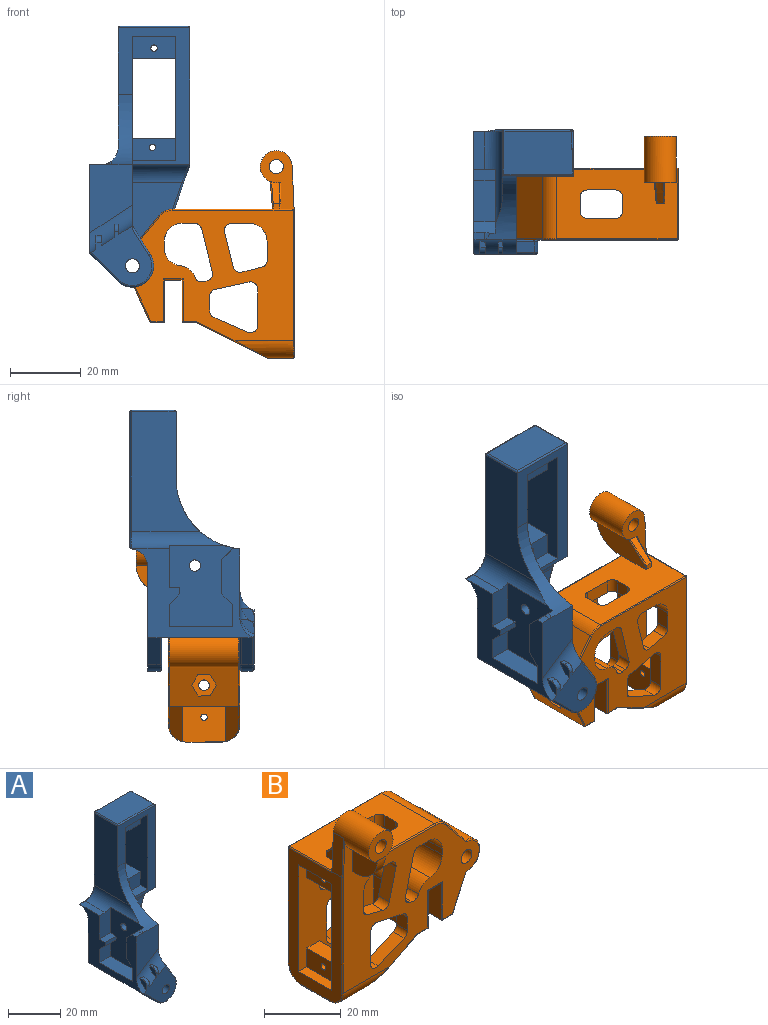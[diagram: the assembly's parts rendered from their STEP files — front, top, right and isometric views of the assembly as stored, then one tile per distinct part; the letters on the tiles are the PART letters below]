
ASSEMBLY  parts=2 mates=1
PART A: 94 faces, bbox 31.5x35.5x74.7 mm
  f0: cylinder r=5mm len=25.96mm, axis (0,1,0), area 138.7mm2, adj f4,f16,f24,f37,f64,f82
  f1: plane 3x2.1mm, normal (0,0,1), area 6.3mm2, adj f3,f12,f15,f67
  f2: plane 29.49x26.47mm, normal (0,1,0), area 568.4mm2, adj f12,f34,f35,f36,f43,f68
  f3: plane 19.15x12mm, normal (0,-1,0), area 182.8mm2, adj f1,f10,f12,f64,f65
  f4: plane 10.6x3mm, normal (0,0,1), area 31.8mm2, adj f0,f12,f16,f83
  f5: plane 29.09x25.27mm, normal (0,-1,0), area 313.8mm2, adj f10,f13,f32,f43,f66,f76,f77,f78
  f6: plane 12.2x6.25mm, normal (0,-1,0), area 73.7mm2, adj f39,f40,f42,f47,f51
  f7: plane 12.2x6.25mm, normal (0,-1,0), area 73.7mm2, adj f38,f39,f42,f48,f50
  f8: plane 22.5x0.08mm, normal (0,1,0), area 1.9mm2, adj f38,f40,f42,f44
  f9: plane 38.94x0.08mm, normal (0,1,0), area 3.2mm2, adj f33,f34,f45,f86
  f10: plane 42.72x26.34mm, normal (1,0,0), area 549.7mm2, adj f3,f5,f26,f27,f28,f29,f30,f31
  f11: cylinder r=1.6mm len=3.2mm, axis (-1,0,0), area 32.2mm2, adj f24,f25
  f12: plane 34.36x25.03mm, normal (-1,0,0), area 317.3mm2, adj f1,f2,f3,f4,f13,f14,f15,f16
  f13: plane 23.21x7.33mm, normal (0,0,-1), area 156.8mm2, adj f5,f12,f32,f63,f74,f78
  f14: plane 9.7x6mm, normal (0,1,0), area 58.2mm2, adj f12,f15,f23,f24
  f15: plane 6.13x3.4mm, normal (0,0.71,0.71), area 26.2mm2, adj f1,f12,f14,f24,f64,f67
  f16: plane 12x6mm, normal (0,-1,0), area 67mm2, adj f0,f4,f12,f17,f24
  f17: plane 6x3mm, normal (0,0,1), area 18mm2, adj f12,f16,f18,f24
  f18: plane 6x1.7mm, normal (0,-1,0), area 10.2mm2, adj f12,f17,f19,f24
  f19: plane 6x3mm, normal (0,-0.71,-0.71), area 25.5mm2, adj f12,f18,f20,f24
  f20: plane 6.3x6mm, normal (0,-1,0), area 37.8mm2, adj f12,f19,f21,f24
  f21: plane 17.8x6mm, normal (0,0,1), area 106.8mm2, adj f12,f20,f22,f24
  f22: plane 6.3x6mm, normal (0,1,0), area 37.8mm2, adj f12,f21,f23,f24
  f23: plane 6x3mm, normal (0,0.71,-0.71), area 25.5mm2, adj f12,f14,f22,f24
  f24: plane 23x18.07mm, normal (-1,0,0), area 352.8mm2, adj f0,f11,f14,f15,f16,f17,f18,f19
  f25: plane 6.81x5.9mm, normal (1,0,0), area 22.1mm2, adj f11,f26,f27,f28,f29,f30,f31
  f26: plane 2.95x2.8mm, normal (0,-0.5,-0.87), area 9.5mm2, adj f10,f25,f27,f31
  f27: plane 2.95x2.8mm, normal (0,0.5,-0.87), area 9.5mm2, adj f10,f25,f26,f28
  f28: plane 3.41x2.8mm, normal (0,1,0), area 9.5mm2, adj f10,f25,f27,f29
  f29: plane 2.95x2.8mm, normal (0,0.5,0.87), area 9.5mm2, adj f10,f25,f28,f30
  f30: plane 2.95x2.8mm, normal (0,-0.5,0.87), area 9.5mm2, adj f10,f25,f29,f31
  f31: plane 3.41x2.8mm, normal (0,-1,0), area 9.5mm2, adj f10,f25,f26,f30
  f32: cylinder r=6mm len=22mm, axis (0,1,0), area 125.4mm2, adj f5,f10,f13,f63
  f33: plane 38.79x8.09mm, normal (1,0,0), area 309.5mm2, adj f9,f34,f49,f75,f88
  f34: plane 30.45x10.53mm, normal (0.95,0,-0.33), area 122.4mm2, adj f2,f9,f33,f35,f45,f68,f75,f76
  f35: cylinder r=6mm len=9.91mm, axis (0,-1,0), area 42.5mm2, adj f2,f34,f36,f77
  f36: plane 7.76x7.74mm, normal (-0.71,0,-0.71), area 38.4mm2, adj f2,f12,f35,f78
  f37: plane 33.7x19.16mm, normal (-1,0,0), area 451.7mm2, adj f0,f49,f64,f80,f92
  f38: plane 12.28x9mm, normal (0,0,1), area 110.2mm2, adj f7,f8,f39,f42,f44,f46
  f39: plane 35x13mm, normal (-1,0,0), area 342.5mm2, adj f6,f7,f38,f40,f46,f47,f48,f49
  f40: plane 12.28x9mm, normal (0,0,-1), area 110.2mm2, adj f6,f8,f39,f42,f44,f46
  f41: plane 19.2x12mm, normal (0,0,1), area 230mm2, adj f86,f87,f88,f90,f91,f92
  f42: plane 35x8mm, normal (1,0,0), area 230mm2, adj f6,f7,f8,f10,f38,f40,f47,f48
  f43: cylinder r=2mm len=4mm, axis (0,-1,0), area 50.3mm2, adj f2,f5
  f44: plane 22.5x5mm, normal (1,0,0), area 112.5mm2, adj f8,f38,f40,f46
  f45: plane 38.94x4.5mm, normal (1,0,0), area 175.1mm2, adj f9,f34,f68,f79,f87
  f46: plane 38.22x21.49mm, normal (0,1,0), area 452.4mm2, adj f38,f39,f40,f44,f50,f51,f79,f80
  f47: plane 12.2x4mm, normal (0,0,-1), area 48.8mm2, adj f6,f39,f42,f49
  f48: plane 12.2x4mm, normal (0,0,1), area 48.8mm2, adj f7,f39,f42,f49
  f49: plane 38.71x20.22mm, normal (0,-1,0), area 275.1mm2, adj f10,f33,f37,f39,f42,f47,f48,f64
  f50: cylinder r=0.9mm len=9mm, axis (0,-1,0), area 50.9mm2, adj f7,f46
  f51: cylinder r=0.9mm len=9mm, axis (0,-1,0), area 50.9mm2, adj f6,f46
  f52: plane 8.14x5.09mm, normal (0.85,0,0.53), area 28.8mm2, adj f10,f60,f69,f72
  f53: plane 3.89x3.5mm, normal (1,0,0), area 5.8mm2, adj f54,f62,f65,f85
  f54: plane 1.74x1.34mm, normal (0,0,1), area 2.1mm2, adj f53,f55,f65,f85
  f55: plane 3.87x3.72mm, normal (-1,0,0), area 8.9mm2, adj f54,f62,f65,f85
  f56: plane 3.76x3.27mm, normal (1,0,0), area 5.2mm2, adj f57,f62,f65,f84
  f57: plane 1.74x1.62mm, normal (0,0,1), area 2.4mm2, adj f56,f58,f65,f84
  f58: plane 3.85x3.71mm, normal (-1,0,0), area 8.9mm2, adj f57,f62,f65,f84
  f59: plane 7.76x7.73mm, normal (-0.71,0,-0.71), area 32.9mm2, adj f12,f60,f71,f74
  f60: cylinder r=6mm len=10.24mm, axis (0,1,0), area 52.5mm2, adj f52,f59,f70,f73
  f61: cylinder r=1.98mm len=4mm, axis (0,1,0), area 49.8mm2, adj f62,f63
  f62: plane 17.07x16.82mm, normal (0,-1,0), area 155.3mm2, adj f10,f53,f55,f56,f58,f61,f65,f69
  f63: plane 16.79x15.88mm, normal (0,1,0), area 113mm2, adj f10,f13,f32,f61,f72,f73,f74
  f64: cylinder r=20mm len=19.9mm, axis (-1,0,0), area 139mm2, adj f0,f3,f10,f15,f24,f37,f49,f67
  f65: cylinder r=5mm len=17.32mm, axis (0.84,0,0.55), area 80.4mm2, adj f3,f10,f12,f53,f54,f55,f56,f57
  f66: cylinder r=5mm len=15.84mm, axis (-1,0,0), area 102.1mm2, adj f5,f10,f49,f75
  f67: cylinder r=5mm len=2.1mm, axis (0,1,0), area 1.7mm2, adj f1,f15,f64
  f68: cylinder r=5mm len=28.12mm, axis (-1,0,0), area 203.7mm2, adj f2,f12,f34,f45,f79,f81
  f69: cylinder r=0.5mm len=8.41mm, axis (0.53,0,-0.85), area 7.2mm2, adj f10,f52,f62,f70
  f70: torus R=5.5mm, axis (0,-1,0), area 13.3mm2, adj f60,f62,f69,f71
  f71: cylinder r=0.5mm len=8.15mm, axis (-0.71,0,0.71), area 8.6mm2, adj f12,f59,f62,f65,f70
  f72: cylinder r=0.5mm len=8.41mm, axis (-0.53,0,0.85), area 7.2mm2, adj f10,f52,f63,f73
  f73: torus R=5.5mm, axis (0,-1,0), area 13.3mm2, adj f60,f63,f72,f74
  f74: cylinder r=0.5mm len=8.11mm, axis (0.71,0,-0.71), area 8.4mm2, adj f13,f59,f63,f73
  f75: bspline ~6.44x5.06mm, area 5mm2, adj f33,f34,f49,f66,f76
  f76: cylinder r=0.5mm len=25.55mm, axis (-0.33,0,-0.95), area 21.1mm2, adj f5,f34,f75,f77
  f77: torus R=5.5mm, axis (0,1,0), area 9.2mm2, adj f5,f35,f76,f78
  f78: cylinder r=0.5mm len=8.12mm, axis (-0.71,0,0.71), area 8.4mm2, adj f5,f13,f36,f77
  f79: cylinder r=0.5mm len=38.73mm, axis (0,0,1), area 30.3mm2, adj f45,f46,f68,f81,f89
  f80: cylinder r=0.5mm len=33.7mm, axis (0,0,-1), area 26.5mm2, adj f37,f46,f82,f93
  f81: cylinder r=0.5mm len=28.11mm, axis (-1,0,0), area 17.4mm2, adj f12,f46,f68,f79,f82,f83
  f82: torus R=5.5mm, axis (0,1,0), area 5.1mm2, adj f0,f46,f80,f81,f83
  f83: cylinder r=0.5mm len=3mm, axis (-1,0,0), area 0.3mm2, adj f4,f12,f81,f82
  f84: cylinder r=2mm len=2mm, axis (1,0,0), area 5mm2, adj f56,f57,f58,f62
  f85: cylinder r=2mm len=2mm, axis (1,0,0), area 4.1mm2, adj f53,f54,f55,f62
  f86: cylinder r=0.5mm len=0.58mm, axis (-1,0,0), area 0.1mm2, adj f9,f41,f87,f88
  f87: cylinder r=0.5mm len=5mm, axis (0,1,0), area 3.7mm2, adj f41,f45,f86,f89
  f88: cylinder r=0.5mm len=8mm, axis (0,1,0), area 5.9mm2, adj f33,f41,f86,f90
  f89: sphere r=0.5mm, area 0.5mm2, adj f79,f87,f91
  f90: cylinder r=0.5mm len=20.2mm, axis (1,0,0), area 15.5mm2, adj f41,f49,f88,f92
  f91: cylinder r=0.5mm len=19.12mm, axis (-1,0,0), area 15mm2, adj f41,f46,f89,f93
  f92: cylinder r=0.5mm len=12.5mm, axis (0,-1,0), area 9.6mm2, adj f37,f41,f90,f93
  f93: sphere r=0.5mm, area 0.2mm2, adj f80,f91,f92
PART B: 139 faces, bbox 51.1x29.6x58.9 mm
  f0: plane 33.98x19.61mm, normal (0,0,1), area 537.5mm2, adj f8,f32,f50,f52,f53,f90,f91,f102
  f1: plane 20.2x19mm, normal (0,0,-1), area 208.1mm2, adj f2,f3,f4,f5,f28,f29,f111,f112
  f2: plane 37.9x28.06mm, normal (0,1,0), area 524.6mm2, adj f1,f9,f10,f11,f13,f20,f21,f22
  f3: plane 50.04x47.58mm, normal (0,-1,0), area 1004.5mm2, adj f1,f10,f12,f25,f28,f29,f30,f31
  f4: plane 37.9x28.07mm, normal (0,-1,0), area 525mm2, adj f1,f9,f10,f11,f13,f20,f21,f22
  f5: plane 50.04x36.7mm, normal (0,1,0), area 975.2mm2, adj f1,f10,f12,f25,f28,f29,f30,f31
  f6: plane 19.6x11mm, normal (0.91,0,-0.41), area 202.6mm2, adj f7,f18,f58,f59,f60,f61,f62,f63
  f7: cylinder r=5mm len=19.6mm, axis (0,1,0), area 307.9mm2, adj f6,f19,f84,f105
  f8: plane 16.8x9.55mm, normal (0,1,0), area 82.5mm2, adj f0,f23,f38,f46,f49,f52,f55,f91
  f9: plane 12.2x5.5mm, normal (-1,0,0), area 64.6mm2, adj f2,f4,f20,f44,f56
  f10: plane 20.2x5.43mm, normal (1,0,0), area 49.6mm2, adj f2,f3,f4,f5,f28,f44,f130,f133
  f11: plane 12.2x10mm, normal (1,0,0), area 119.4mm2, adj f2,f4,f24,f45,f57,f73,f74
  f12: plane 20.2x2mm, normal (-1,0,0), area 40.4mm2, adj f3,f5,f29,f30
  f13: plane 12.2x11.05mm, normal (-1,0,0), area 127.7mm2, adj f2,f4,f14,f27,f31
  f14: plane 19.6x4mm, normal (0,0,-1), area 78.4mm2, adj f13,f15,f36,f41,f77,f97
  f15: plane 19.6x12mm, normal (1,0,0), area 228.1mm2, adj f14,f16,f27,f78,f98
  f16: plane 19.6x5mm, normal (0,0,-1), area 98mm2, adj f15,f17,f79,f99
  f17: plane 19.6x12mm, normal (-1,0,0), area 228.1mm2, adj f16,f18,f26,f80,f100
  f18: plane 19.6x4mm, normal (0,0,-1), area 78.4mm2, adj f6,f17,f81,f101
  f19: plane 19.6x9.17mm, normal (0.77,0,0.63), area 232.1mm2, adj f7,f32,f86,f106
  f20: plane 12.2x3mm, normal (0,0,-1), area 36.6mm2, adj f2,f4,f9,f23
  f21: plane 12.2x6mm, normal (-1,0,0), area 70.7mm2, adj f2,f4,f22,f45,f57
  f22: plane 12.2x3mm, normal (0,0,1), area 36.6mm2, adj f2,f4,f21,f23
  f23: plane 41.7x19.6mm, normal (-1,0,0), area 388.3mm2, adj f2,f4,f8,f20,f22,f38,f85,f87
  f24: plane 10.2x7.34mm, normal (0,0,-1), area 74.8mm2, adj f11,f73,f74,f89
  f25: cylinder r=2mm len=20.2mm, axis (0,1,0), area 253.8mm2, adj f3,f5
  f26: cylinder r=1.5mm len=4mm, axis (-1,0,0), area 37.7mm2, adj f17,f64
  f27: cylinder r=1.5mm len=4mm, axis (-1,0,0), area 37.7mm2, adj f13,f15
  f28: cylinder r=5mm len=20.2mm, axis (0,-1,0), area 155.8mm2, adj f1,f3,f5,f10,f56
  f29: cylinder r=5mm len=20.2mm, axis (0,1,0), area 158.7mm2, adj f1,f3,f5,f12
  f30: cylinder r=5mm len=20.2mm, axis (0,-1,0), area 148.5mm2, adj f3,f5,f12,f31
  f31: cylinder r=5mm len=20.2mm, axis (0,-1,0), area 134.3mm2, adj f2,f3,f4,f5,f13,f30,f127,f136
  f32: cylinder r=5mm len=19.6mm, axis (0,-1,0), area 86.7mm2, adj f0,f19,f88,f104
  f33: plane 12.24x4mm, normal (0.97,0,-0.24), area 50.4mm2, adj f2,f3,f135,f137
  f34: plane 9.82x4mm, normal (-0.97,0,0.24), area 40.5mm2, adj f2,f3,f134,f138
  f35: plane 5.61x4mm, normal (0.24,0,0.97), area 23.1mm2, adj f2,f3,f133,f138
  f36: plane 19.72x9.86mm, normal (0.45,0,-0.89), area 72mm2, adj f2,f14,f95,f96
  f37: plane 4x1.05mm, normal (0.24,0,0.97), area 4.3mm2, adj f2,f3,f136,f137
  f38: plane 12.2x3.7mm, normal (-1,0,0.05), area 45.2mm2, adj f8,f23,f46,f83
  f39: plane 4x1.04mm, normal (0.24,0,0.97), area 4.3mm2, adj f4,f5,f127,f132
  f40: plane 9.82x4mm, normal (-0.97,0,0.24), area 40.5mm2, adj f4,f5,f129,f131
  f41: plane 19.72x9.86mm, normal (0.45,0,-0.89), area 72mm2, adj f4,f14,f75,f76
  f42: plane 5.6x4mm, normal (0.24,0,0.97), area 23.1mm2, adj f4,f5,f130,f131
  f43: plane 12.25x4mm, normal (0.97,0,-0.24), area 50.5mm2, adj f4,f5,f128,f132
  f44: plane 12.2x4.64mm, normal (0,0,-1), area 56.6mm2, adj f2,f4,f9,f10
  f45: plane 12.2x4.64mm, normal (0,0,1), area 56.6mm2, adj f2,f4,f11,f21
  f46: cylinder r=4.5mm len=13mm, axis (0,1,0), area 303.8mm2, adj f3,f8,f38,f47,f50,f51,f54,f83
  f47: plane 9x7.7mm, normal (-1,0,0), area 55.9mm2, adj f3,f46,f48,f54
  f48: plane 2.38x1.1mm, normal (0,0,-1), area 2.6mm2, adj f3,f47,f50,f54
  f49: cylinder r=2mm len=13mm, axis (0,1,0), area 163.4mm2, adj f8,f51
  f50: plane 18.71x8.15mm, normal (1,0,-0.08), area 113.2mm2, adj f0,f3,f46,f48,f54,f102,f109,f110
  f51: plane 9x8.6mm, normal (0,-1,0), area 50.1mm2, adj f46,f49,f54
  f52: plane 7.19x5.7mm, normal (-1,0,0), area 24.5mm2, adj f0,f8,f107,f108
  f53: plane 1.91x1.55mm, normal (0,1,0), area 2.8mm2, adj f0,f55,f107,f108,f109,f110
  f54: cylinder r=7.9mm len=7.9mm, axis (-1,0,0), area 32.6mm2, adj f46,f47,f48,f50,f51
  f55: cone r=10.5mm half-angle=45deg, axis (0,1,0), area 20.7mm2, adj f8,f53,f108,f110
  f56: cylinder r=0.9mm len=5.57mm, axis (-1,0,0), area 31.5mm2, adj f9,f28
  f57: cylinder r=0.9mm len=4.64mm, axis (-1,0,0), area 26.2mm2, adj f11,f21
  f58: plane 2.97x2.7mm, normal (0,0.86,0.52), area 7mm2, adj f6,f59,f63,f64
  f59: plane 4.08x3.03mm, normal (0,0.87,-0.48), area 11.7mm2, adj f6,f58,f60,f64
  f60: plane 4.1x3.46mm, normal (0,0.02,-1), area 14.2mm2, adj f6,f59,f61,f64
  f61: plane 4.1x2.97mm, normal (0,-0.86,-0.52), area 11.9mm2, adj f6,f60,f62,f64
  f62: plane 3.03x2.76mm, normal (0,-0.87,0.48), area 7.2mm2, adj f6,f61,f63,f64
  f63: plane 3.46x1.38mm, normal (0,-0.02,1), area 4.7mm2, adj f6,f58,f62,f64
  f64: plane 6.93x6.06mm, normal (1,0,0), area 24.1mm2, adj f26,f58,f59,f60,f61,f62,f63
  f65: plane 10.36x4mm, normal (1,0,0), area 41.4mm2, adj f4,f5,f121,f122
  f66: plane 9.52x4.13mm, normal (-0.4,0,0.92), area 41.5mm2, adj f4,f5,f120,f122
  f67: plane 4.15x4mm, normal (-1,0,0), area 16.6mm2, adj f4,f5,f119,f120
  f68: plane 9.52x4mm, normal (-0.21,0,-0.98), area 39mm2, adj f4,f5,f119,f121
  f69: plane 9.52x4mm, normal (-0.21,0,-0.98), area 39mm2, adj f2,f3,f123,f126
  f70: plane 4.15x4mm, normal (-1,0,0), area 16.6mm2, adj f2,f3,f123,f124
  f71: plane 9.52x4.13mm, normal (-0.4,0,0.92), area 41.5mm2, adj f2,f3,f124,f125
  f72: plane 10.36x4mm, normal (1,0,0), area 41.4mm2, adj f2,f3,f125,f126
  f73: cylinder r=5mm len=16.67mm, axis (-1,0,0), area 83.9mm2, adj f4,f5,f11,f24,f75,f92
  f74: cylinder r=5mm len=16.67mm, axis (-1,0,0), area 83.9mm2, adj f2,f3,f11,f24,f87,f95
  f75: bspline ~11.16x5.86mm, area 3.6mm2, adj f4,f41,f73,f76
  f76: cylinder r=0.3mm len=10.73mm, axis (0.89,0,0.45), area 5.6mm2, adj f5,f41,f75,f77
  f77: cylinder r=0.3mm len=4.07mm, axis (-1,0,0), area 1.8mm2, adj f5,f14,f76,f78
  f78: cylinder r=0.3mm len=12.3mm, axis (0,0,-1), area 5.7mm2, adj f5,f15,f77,f79
  f79: cylinder r=0.3mm len=5.6mm, axis (-1,0,0), area 2.5mm2, adj f5,f16,f78,f80
  f80: cylinder r=0.3mm len=12.3mm, axis (0,0,1), area 5.7mm2, adj f5,f17,f79,f81
  f81: cylinder r=0.3mm len=4mm, axis (-1,0,0), area 1.8mm2, adj f5,f18,f80,f82
  f82: cylinder r=0.3mm len=11.3mm, axis (0.41,0,0.91), area 5.7mm2, adj f5,f6,f81,f84
  f83: cylinder r=0.3mm len=12.22mm, axis (0.05,0,1), area 5.4mm2, adj f3,f38,f46,f85
  f84: torus R=4.7mm, axis (0,1,0), area 7.3mm2, adj f5,f7,f82,f86
  f85: cylinder r=0.3mm len=37mm, axis (0,0,1), area 17.4mm2, adj f3,f23,f83,f87
  f86: cylinder r=0.3mm len=9.47mm, axis (0.63,0,-0.77), area 5.6mm2, adj f5,f19,f84,f88
  f87: torus R=4.7mm, axis (-1,0,0), area 3.6mm2, adj f23,f74,f85,f89
  f88: torus R=4.7mm, axis (0,1,0), area 2mm2, adj f5,f32,f86,f90
  f89: cylinder r=0.3mm len=10.2mm, axis (0,1,0), area 4.8mm2, adj f23,f24,f87,f92
  f90: cylinder r=0.3mm len=33.97mm, axis (1,0,0), area 16mm2, adj f0,f5,f88,f93
  f91: cylinder r=0.3mm len=15.9mm, axis (0,-1,0), area 7.5mm2, adj f0,f8,f23,f93
  f92: torus R=4.7mm, axis (-1,0,0), area 3.6mm2, adj f23,f73,f89,f94
  f93: sphere r=0.3mm, area 0.2mm2, adj f90,f91,f94
  f94: cylinder r=0.3mm len=36.7mm, axis (0,0,1), area 17.3mm2, adj f5,f23,f92,f93
  f95: bspline ~11.16x5.86mm, area 3.6mm2, adj f2,f36,f74,f96
  f96: cylinder r=0.3mm len=10.73mm, axis (-0.89,0,-0.45), area 5.6mm2, adj f3,f36,f95,f97
  f97: cylinder r=0.3mm len=4.07mm, axis (-1,0,0), area 1.8mm2, adj f3,f14,f96,f98
  f98: cylinder r=0.3mm len=12.3mm, axis (0,0,-1), area 5.7mm2, adj f3,f15,f97,f99
  f99: cylinder r=0.3mm len=5.6mm, axis (-1,0,0), area 2.5mm2, adj f3,f16,f98,f100
  f100: cylinder r=0.3mm len=12.3mm, axis (0,0,1), area 5.7mm2, adj f3,f17,f99,f101
  f101: cylinder r=0.3mm len=4mm, axis (-1,0,0), area 1.8mm2, adj f3,f18,f100,f103
  f102: cylinder r=0.3mm len=28.2mm, axis (1,0,0), area 13.3mm2, adj f0,f3,f50,f104
  f103: cylinder r=0.3mm len=11.3mm, axis (0.41,0,0.91), area 5.7mm2, adj f3,f6,f101,f105
  f104: torus R=4.7mm, axis (0,-1,0), area 2mm2, adj f3,f32,f102,f106
  f105: torus R=4.7mm, axis (0,-1,0), area 7.3mm2, adj f3,f7,f103,f106
  f106: cylinder r=0.3mm len=9.47mm, axis (0.63,0,-0.77), area 5.6mm2, adj f3,f19,f104,f105
  f107: cylinder r=0.3mm len=1.55mm, axis (0,0,1), area 0.7mm2, adj f0,f52,f53,f108
  f108: bspline ~10.51x10.38mm, area 4.2mm2, adj f8,f52,f53,f55,f107
  f109: cylinder r=0.3mm len=1.56mm, axis (0.08,0,1), area 0.7mm2, adj f0,f50,f53,f110
  f110: bspline ~8.66x8.38mm, area 4.6mm2, adj f46,f50,f53,f55,f109
  f111: plane 4x4mm, normal (-1,0,0), area 16mm2, adj f0,f1,f115,f118
  f112: plane 8x4mm, normal (0,-1,0), area 32mm2, adj f0,f1,f115,f116
  f113: plane 4x4mm, normal (1,0,0), area 16mm2, adj f0,f1,f116,f117
  f114: plane 8x4mm, normal (0,1,0), area 32mm2, adj f0,f1,f117,f118
  f115: cylinder r=2mm len=4mm, axis (0,0,1), area 12.6mm2, adj f0,f1,f111,f112
  f116: cylinder r=2mm len=4mm, axis (0,0,-1), area 12.6mm2, adj f0,f1,f112,f113
  f117: cylinder r=2mm len=4mm, axis (0,0,1), area 12.6mm2, adj f0,f1,f113,f114
  f118: cylinder r=2mm len=4mm, axis (0,0,-1), area 12.6mm2, adj f0,f1,f111,f114
  f119: cylinder r=2mm len=4mm, axis (0,-1,0), area 10.8mm2, adj f4,f5,f67,f68
  f120: cylinder r=2mm len=4mm, axis (0,-1,0), area 9.3mm2, adj f4,f5,f66,f67
  f121: cylinder r=2mm len=4mm, axis (0,-1,0), area 14.3mm2, adj f4,f5,f65,f68
  f122: cylinder r=2mm len=4mm, axis (0,-1,0), area 15.8mm2, adj f4,f5,f65,f66
  f123: cylinder r=2mm len=4mm, axis (0,-1,0), area 10.8mm2, adj f2,f3,f69,f70
  f124: cylinder r=2mm len=4mm, axis (0,-1,0), area 9.3mm2, adj f2,f3,f70,f71
  f125: cylinder r=2mm len=4mm, axis (0,-1,0), area 15.8mm2, adj f2,f3,f71,f72
  f126: cylinder r=2mm len=4mm, axis (0,-1,0), area 14.3mm2, adj f2,f3,f69,f72
  f127: cylinder r=2mm len=4mm, axis (0,-1,0), area 11.7mm2, adj f4,f5,f31,f39
  f128: cylinder r=2mm len=4mm, axis (0,1,0), area 10.6mm2, adj f1,f4,f5,f43
  f129: cylinder r=2mm len=4mm, axis (0,1,0), area 14.5mm2, adj f1,f4,f5,f40
  f130: cylinder r=2mm len=4mm, axis (0,1,0), area 10.6mm2, adj f4,f5,f10,f42
  f131: cylinder r=2mm len=4mm, axis (0,1,0), area 12.6mm2, adj f4,f5,f40,f42
  f132: cylinder r=2mm len=4mm, axis (0,1,0), area 12.6mm2, adj f4,f5,f39,f43
  f133: cylinder r=2mm len=4mm, axis (0,1,0), area 10.6mm2, adj f2,f3,f10,f35
  f134: cylinder r=2mm len=4mm, axis (0,-1,0), area 14.5mm2, adj f1,f2,f3,f34
  f135: cylinder r=2mm len=4mm, axis (0,1,0), area 10.6mm2, adj f1,f2,f3,f33
  f136: cylinder r=2mm len=4mm, axis (0,-1,0), area 11.7mm2, adj f2,f3,f31,f37
  f137: cylinder r=2mm len=4mm, axis (0,-1,0), area 12.6mm2, adj f2,f3,f33,f37
  f138: cylinder r=2mm len=4mm, axis (0,1,0), area 12.6mm2, adj f2,f3,f34,f35
PLACE A t=(-47.18,-1.43,58.06)mm
PLACE B rot(axis=(0,0,1),180deg) t=(-47.18,-2.33,54.57)mm
MATE slider B.f25 <-> A.f32  axis (0,-1,0) through (-47.18,-12.43,54.57)mm
